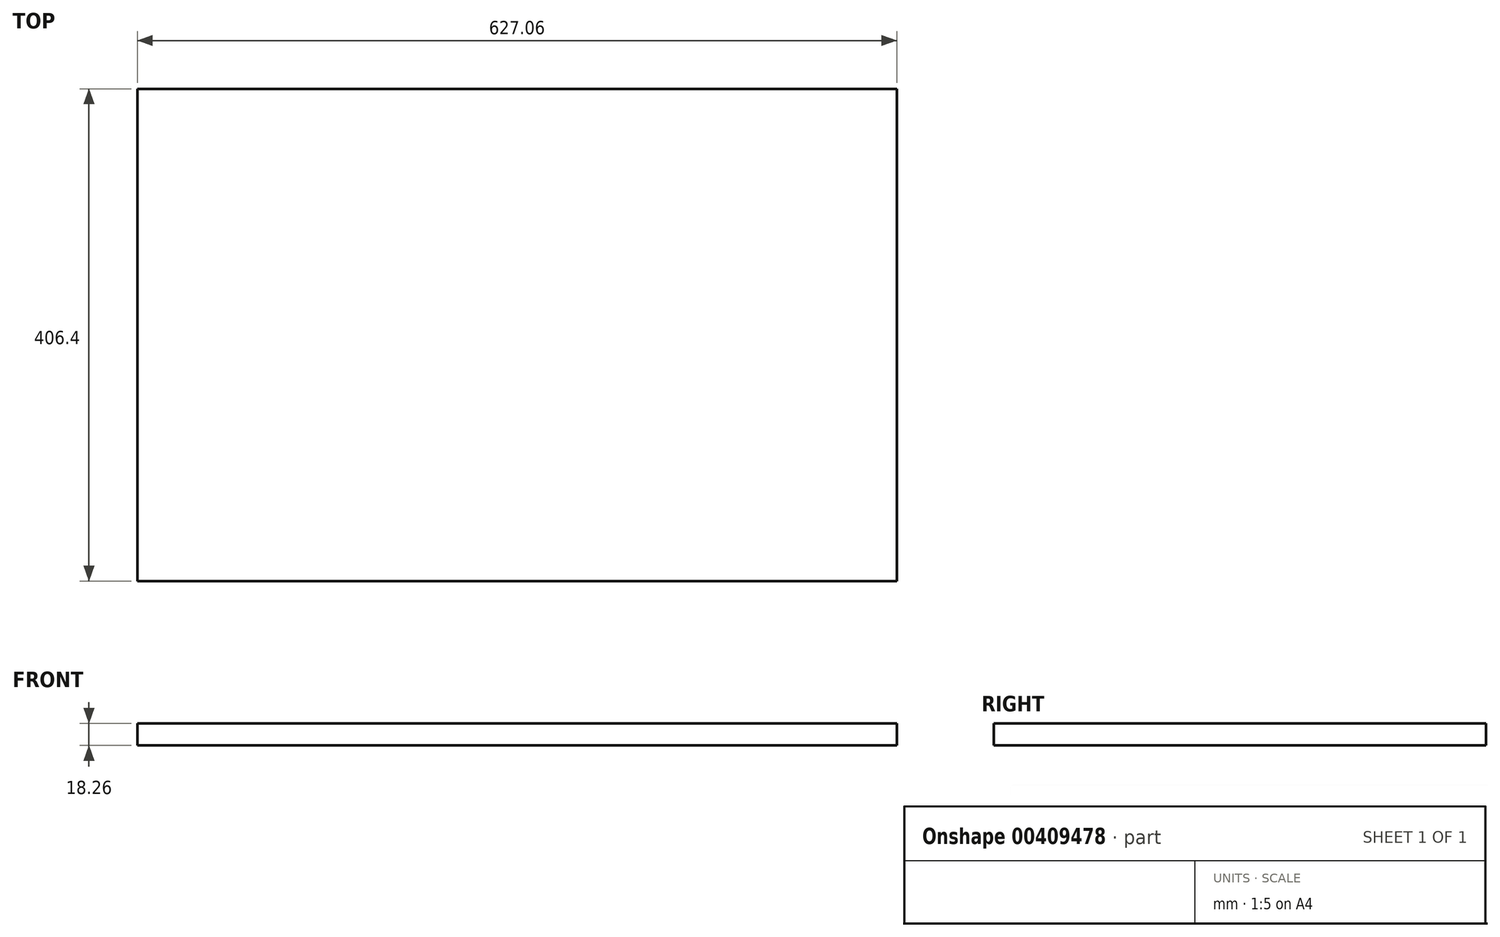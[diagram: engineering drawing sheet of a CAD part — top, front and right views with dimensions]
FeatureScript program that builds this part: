
annotation { "Feature Type Name" : "Feature", "Feature Type Description" : "" }
export const myFeature = defineFeature(function(context is Context, id is Id, definition is map)
    precondition{}
    {
        {
            var Q0;
            Q0=qCreatedBy(makeId("Front.planeOp"),FACE);
            var sketch = newSketch(context, id + "F0", { "sketchPlane" : qUnion([Q0])});
            skLineSegment(sketch, "E0.bottom", {"start": v(0, 0) * mm, "end": v(627.06, 0) * mm});
            skLineSegment(sketch, "E0.top", {"start": v(0, 18.26) * mm, "end": v(627.06, 18.26) * mm});
            skLineSegment(sketch, "E0.left", {"start": v(0, 0) * mm, "end": v(0, 18.26) * mm});
            skLineSegment(sketch, "E0.right", {"start": v(627.06, 0) * mm, "end": v(627.06, 18.26) * mm});
            skSolve(sketch);
        }
        {
            var Q0;
            Q0=makeQuery(id+"F0.imprint","IMPRINT",FACE,{"disambiguationData":[TD([[makeQuery(id+"F0.imprint","IMPRINT",EDGE,{"derivedFrom":sQuery(id+"F0.wireOp",EDGE,"E0.bottom")}),1.0]])]});
            extrude(context, id + "F1", {"entities" : qUnion([Q0]), "depth" : 406.4 * mm});
        }
    });
